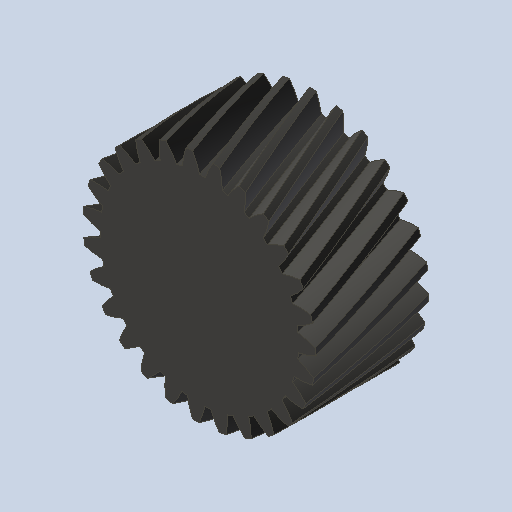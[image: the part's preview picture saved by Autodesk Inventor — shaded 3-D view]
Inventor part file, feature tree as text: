
AUTODESK INVENTOR PART (.ipt)
format: ipt  version: 2023 (Build 270158000, 158)  size: 507,392 bytes
history: native  units: mm (DEFAULTED — no unit token found)
features: plane x3, other x3, sketch x2, extrude x1
ambient origin geometry x8: Origin, YZ Plane, XZ Plane, XY Plane, X Axis, Y Axis, Z Axis, Center Point
bodies: Solid1 (feature_tree)
feature tree (9):
  extrude  "Extrusion1"  Depth=15.0mm TaperAngle=0.0deg
  plane  "Work Plane2"
  plane  "Work Plane8"
  plane  "Work Plane9"
  other  "Spur Gear"
  sketch  "Sketch1"  dims[d0=30.7328mm d1=15.0mm d2=0.0mm]
  sketch  "Sketch2"  dims[d3=28.7328mm d4=10.0mm d5=0.0mm d16=101.6mm d17=0.0mm d34=1.163553mm d39=0.0mm d41=0.0mm d43=101.6mm d46=101.6mm d47=0.0mm d48=0.0mm]
  other  "Srf1"
  other  "Pitch Diameter"
